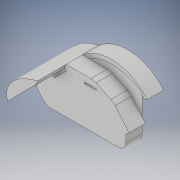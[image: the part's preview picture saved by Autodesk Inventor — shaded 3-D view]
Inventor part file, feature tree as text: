
AUTODESK INVENTOR PART (.ipt)
format: ipt  version: 2017 (Build 210142000, 142)  size: 601,088 bytes
history: native  units: mm
features: sketch x30, extrude x26, plane x7, other x3, fillet x3, revolve x1, boolean_combine x1
ambient origin geometry x8: Origin, YZ Plane, XZ Plane, XY Plane, X Axis, Y Axis, Z Axis, Center Point
bodies: Solid1 (feature_tree), Solid2 (feature_tree)
feature tree (71):
  extrude  "Extrusion1"  Depth=60.0mm
  plane  "Work Plane1"
  extrude  "Extrusion2"  Depth=60.0mm
  other  "Bend Part1"
  other  "Bend Part2"
  extrude  "Extrusion3"  Depth=32.454mm
  plane  "Work Plane2"
  extrude  "Extrusion4"  Depth=20.0mm
  other  "Bend Part3"
  extrude  "Extrusion5"  Depth=30.0mm
  revolve  "Revolution1"  [1 undecoded]
  plane  "Work Plane3"
  extrude  "Extrusion6"  Depth=10.0mm
  boolean_combine  "Combine1"
  plane  "Work Plane4"
  extrude  "Extrusion7"  TaperAngle=90.0deg  [1 undecoded]
  extrude  "Extrusion8"  Depth=80.0mm
  extrude  "Extrusion9"  Depth=50.0mm TaperAngle=135.0deg
  extrude  "Extrusion10"  Depth=60.0mm
  plane  "Work Plane5"
  extrude  "Extrusion11"  Depth=60.0mm
  extrude  "Extrusion12"  Depth=60.0mm
  plane  "Work Plane6"
  extrude  "Extrusion13"  [1 undecoded]
  extrude  "Extrusion14"  Depth=30.0mm TaperAngle=0.0deg
  plane  "Work Plane7"
  extrude  "Extrusion15"  Depth=20.0mm TaperAngle=0.0deg
  extrude  "Extrusion16"  Depth=15.219936mm
  extrude  "Extrusion17"  Depth=15.155142mm
  fillet  "Fillet1"  Radius=20.0mm
  extrude  "Extrusion18"  Depth=60.0mm
  fillet  "Fillet2"  Radius=43.193283mm
  fillet  "Fillet3"  Radius=60.0mm
  extrude  "Extrusion19"  Depth=14.497104mm
  extrude  "Extrusion20"  Depth=104.0mm TaperAngle=0.0deg
  extrude  "Extrusion21"  [1 undecoded]
  extrude  "Extrusion22"  Depth=1.164325mm
  extrude  "Extrusion23"  Depth=25.536883mm
  extrude  "Extrusion24"  TaperAngle=0.0deg  [1 undecoded]
  extrude  "Extrusion25"  Depth=50.209mm
  extrude  "Extrusion26"  Depth=95.197mm TaperAngle=0.0deg
  sketch  "Sketch1"  dims[d0=60.0mm d1=35.0mm]
  sketch  "Sketch2"  dims[d2=60.0mm d3=33.005006mm]
  sketch  "Sketch3"  dims[d4=75.0mm d5=0.0mm d6=32.454mm]
  sketch  "Sketch4"  dims[d7=85.0mm d8=20.0mm]
  sketch  "Sketch5"  dims[d9=5.0mm d10=0.0mm d11=30.0mm]
  sketch  "Sketch6"  dims[d12=55.0mm d13=10.0mm d14=4.363323mm]
  sketch  "Sketch7"  dims[d15=20.0mm d16=10.0mm d17=4.363323mm]
  sketch  "Sketch8"  dims[d18=20.0mm d19=0.0mm d20=90.0deg]
  sketch  "Sketch9"  dims[d21=20.0mm d22=80.0mm]
  sketch  "Sketch10"  dims[d23=5.0mm d24=0.0mm d25=50.0mm d26=135.0deg]
  sketch  "Sketch11"  dims[d27=60.0mm d28=35.0mm]
  sketch  "Sketch12"  dims[d29=35.0mm d30=60.0mm]
  sketch  "Sketch13"  dims[d31=20.0mm d32=0.0mm d33=60.0mm]
  sketch  "Sketch14"  dims[d34=270.0deg d35=-4.697mm]
  sketch  "Sketch15"  dims[d36=20.0mm d37=30.0mm d38=0.0mm]
  sketch  "Sketch16"  dims[d39=-20.0mm d40=20.0mm d41=0.0mm]
  sketch  "Sketch17"  dims[d42=35.67mm d43=15.219936mm]
  sketch  "Sketch18"  dims[d44=35.67mm d45=15.155142mm d46=20.0mm d47=0.0mm]
  sketch  "Sketch19"  dims[d48=20.0mm d49=0.0mm d50=100.334153mm d51=43.193283mm d52=60.0mm d53=0.0mm]
  sketch  "Sketch20"  dims[d54=60.5mm d55=14.497104mm]
  sketch  "Sketch21"  dims[d56=25.287025mm d57=104.0mm d58=0.0mm]
  sketch  "Sketch22"  dims[d59=2.439mm d60=0.0mm d61=-31.25mm]
  sketch  "Sketch23"  dims[d62=0.980484mm d63=1.164325mm]
  sketch  "Sketch24"  dims[d64=2.246206mm d65=25.536883mm]
  sketch  "Sketch25"  dims[d66=100.0mm d67=0.0mm d68=0.0mm]
  sketch  "Sketch26"  dims[d69=5.0mm d70=0.0mm d71=50.209mm]
  sketch  "Sketch27"  dims[d72=95.197mm d73=0.0mm d74=95.197mm d75=0.0mm]
  sketch  "Sketch28"  dims[d76=60.0mm]
  sketch  "Sketch29"  dims[d77=60.0mm]
  sketch  "Sketch30"  dims[d78=20.0mm d79=18.461mm d80=116.447mm d81=0.0mm d82=10.0mm d83=8.797686mm d84=116.447mm d85=0.0mm d86=10.0mm d87=9.0mm d89=60.197145mm d90=34.482005mm d91=20.0mm d92=3.0mm d93=20.0mm d94=90.0deg d95=55.512917mm d96=23.386841mm d97=11.976391mm d98=75.0mm d99=0.0mm d100=3.0mm d101=20.0mm d102=75.0mm d103=0.0mm d104=14.0mm d105=2.0mm d106=75.0mm d107=0.0mm d108=20.0mm d109=0.0mm d110=20.0mm d111=0.0mm d112=20.0mm d113=0.0mm d114=20.0mm d115=0.0mm d116=20.0mm d117=60.0mm d118=10.0mm d119=0.0mm]
note: 5 required parameter values undecoded (feature->parameter linkage not recoverable at this tier; creation-order binding heuristic only, values carry confidence <= 0.55)